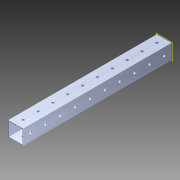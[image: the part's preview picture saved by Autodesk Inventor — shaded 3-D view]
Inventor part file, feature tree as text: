
AUTODESK INVENTOR PART (.ipt)
format: ipt  version: 2014 (Build 180170000, 170)  size: 1,232,896 bytes
history: native  units: in
note: dims shown in document units (in); Inventor stores cm internally (conversion verified against a paired STEP export)
features: extrude x3, sketch x3, pattern_circular x1, other x1, plane x1, imported_body x1
ambient origin geometry x8: Origin, YZ Plane, XZ Plane, XY Plane, X Axis, Y Axis, Z Axis, Center Point
bodies: Body1 (feature_tree)
feature tree (10):
  pattern_circular  "CirPattern2"
  other  "217-3426-STEP1"
  plane  "Work Plane1"
  extrude  "Extrusion1"  Depth=3937.0079in TaperAngle=0.0deg
  extrude  "Extrusion2"  Depth=10.0in TaperAngle=0.0deg
  extrude  "Extrusion3"  [1 undecoded]
  imported_body  "Base1"
  sketch  "Sketch1"  dims[d0=-21.0in d1=3937.0079in d2=0.0in]
  sketch  "Sketch3"  dims[d3=1.0in d4=0.0in d5=10.0in d6=0.0in]
  sketch  "Sketch4"
note: 1 required parameter value undecoded (feature->parameter linkage not recoverable at this tier; creation-order binding heuristic only, values carry confidence <= 0.55)
